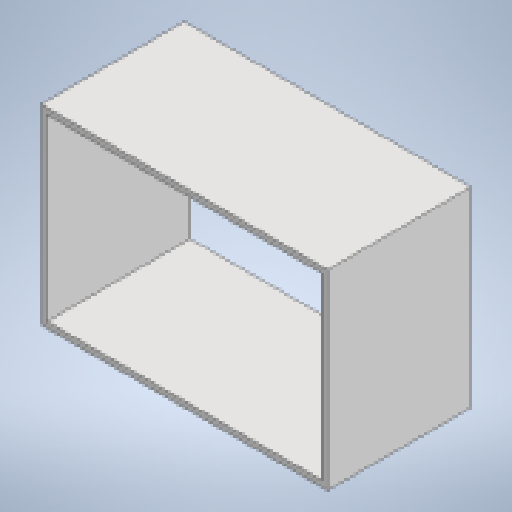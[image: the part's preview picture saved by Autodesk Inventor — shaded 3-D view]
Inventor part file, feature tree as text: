
AUTODESK INVENTOR PART (.ipt)
format: ipt  version: 2023 (Build 270158000, 158)  size: 129,024 bytes
history: native  units: in
note: dims shown in document units (in); Inventor stores cm internally (conversion verified against a paired STEP export)
features: extrude x2, sketch x2, shell x1
ambient origin geometry x8: Origin, YZ Plane, XZ Plane, XY Plane, X Axis, Y Axis, Z Axis, Center Point
bodies: Solid1 (feature_tree)
feature tree (5):
  extrude  "Extrusion1"  Depth=4.0in
  shell  "Shell1"  Thickness=1.575in
  extrude  "Extrusion2"  Depth=1.575in
  sketch  "Sketch1"  dims[d0=6.0in d1=4.0in d2=1.575in d3=0.0in]
  sketch  "Sketch2"  dims[d4=0.125in d5=0.315in d6=0.9843in d7=3.5433in d8=1.575in d9=0.0in]
